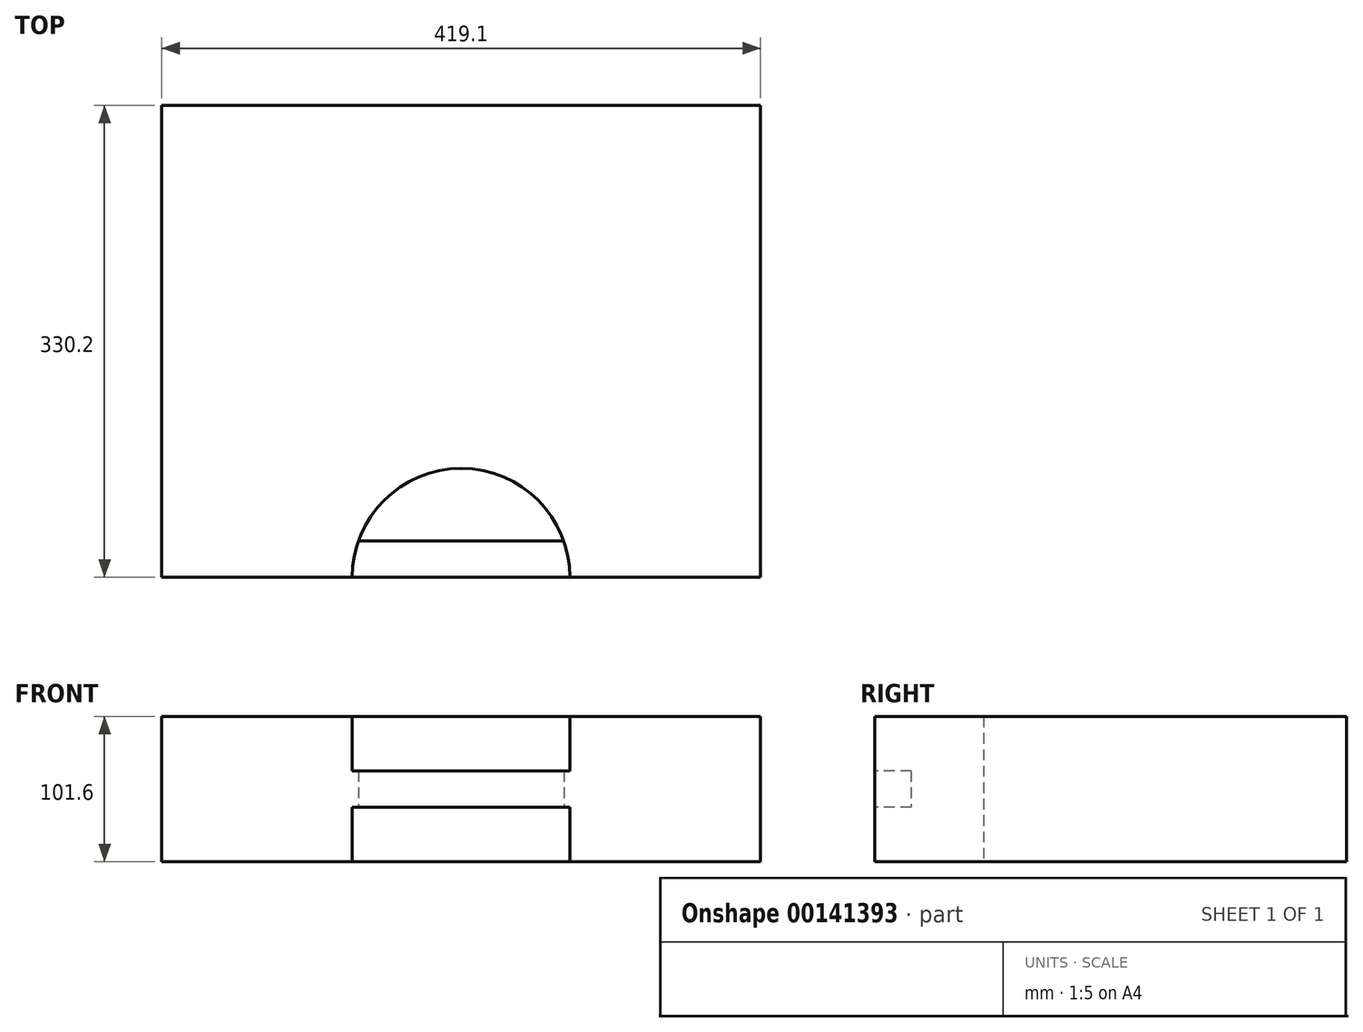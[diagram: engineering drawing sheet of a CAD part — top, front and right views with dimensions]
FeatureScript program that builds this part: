
annotation { "Feature Type Name" : "Feature", "Feature Type Description" : "" }
export const myFeature = defineFeature(function(context is Context, id is Id, definition is map)
    precondition{}
    {
        {
            var Q0;
            Q0=qCreatedBy(makeId("Top.planeOp"),FACE);
            var sketch = newSketch(context, id + "F0", { "sketchPlane" : qUnion([Q0])});
            skLineSegment(sketch, "E0.bottom", {"start": v(-209.55, 165.1) * mm, "end": v(209.55, 165.1) * mm});
            skLineSegment(sketch, "E0.top", {"start": v(-209.55, -165.1) * mm, "end": v(209.55, -165.1) * mm});
            skLineSegment(sketch, "E0.left", {"start": v(-209.55, 165.1) * mm, "end": v(-209.55, -165.1) * mm});
            skLineSegment(sketch, "E0.right", {"start": v(209.55, 165.1) * mm, "end": v(209.55, -165.1) * mm});
            skPoint(sketch, "E0.middle", {"position": v(0, 0) * mm});
            skArc(sketch, "E1", {"start": v(76.2, -165.1) * mm, "mid": v(0, -88.9) * mm, "end": v(-76.2, -165.1) * mm});
            skSolve(sketch);
        }
        {
            var Q0;
            Q0=makeQuery(id+"F0.imprint","IMPRINT",FACE,{"disambiguationData":[TD([[makeQuery(id+"F0.imprint","IMPRINT",EDGE,{"derivedFrom":sQuery(id+"F0.wireOp",EDGE,"E0.bottom")}),-1.0]])]});
            extrude(context, id + "F1", {"entities" : qUnion([Q0]), "depth" : 101.6 * mm});
        }
        {
            var Q0;
            {var subQ0=sQuery(id+"F0.wireOp",EDGE,"E0.top");Q0=makeQuery(id+"F1.opExtrude","SWEPT_FACE",FACE,{"disambiguationData":[OSD([subQ0]),TDD([makeQuery(id+"F0.imprint","IMPRINT",EDGE,{"disambiguationData":[TD([[makeQuery(id+"F0.imprint","INTERSECT",VERTEX,{"derivedFrom":[subQ0,sQuery(id+"F0.wireOp",EDGE,"E0.left")]}),-1.0]])],"derivedFrom":subQ0})])]});}
            var sketch = newSketch(context, id + "F2", { "sketchPlane" : qUnion([Q0])});
            skLineSegment(sketch, "E2.bottom", {"start": v(-76.2, 63.5) * mm, "end": v(76.2, 63.5) * mm});
            skLineSegment(sketch, "E2.top", {"start": v(-76.2, 38.1) * mm, "end": v(76.2, 38.1) * mm});
            skLineSegment(sketch, "E2.left", {"start": v(-76.2, 63.5) * mm, "end": v(-76.2, 38.1) * mm});
            skLineSegment(sketch, "E2.right", {"start": v(76.2, 63.5) * mm, "end": v(76.2, 38.1) * mm});
            skSolve(sketch);
        }
        {
            var Q0;
            Q0 = qSketchRegion(id + "F2", true);
            extrude(context, id + "F3", {"entities" : qUnion([Q0]), "operationType" : NewBodyOperationType.ADD, "oppositeDirection" : true, "depth" : 25.4 * mm});
        }
    });
